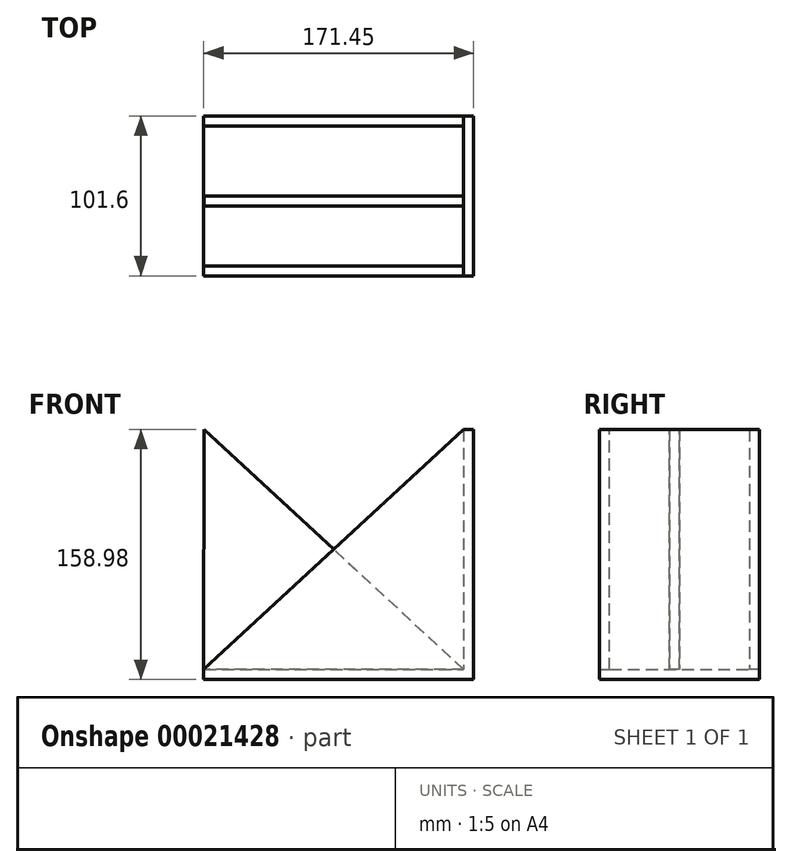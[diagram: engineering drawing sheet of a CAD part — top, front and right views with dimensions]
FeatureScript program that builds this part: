
annotation { "Feature Type Name" : "Feature", "Feature Type Description" : "" }
export const myFeature = defineFeature(function(context is Context, id is Id, definition is map)
    precondition{}
    {
        {
            var Q0;
            Q0=qCreatedBy(makeId("Front.planeOp"),FACE);
            var sketch = newSketch(context, id + "F0", { "sketchPlane" : qUnion([Q0])});
            skLineSegment(sketch, "E0", {"start": v(99.3, 82.76) * mm, "end": v(99.3, -69.64) * mm});
            skLineSegment(sketch, "E1", {"start": v(99.3, -69.64) * mm, "end": v(-65.8, -69.64) * mm});
            skLineSegment(sketch, "E2", {"start": v(-65.8, -69.64) * mm, "end": v(99.3, 82.76) * mm});
            skSolve(sketch);
        }
        {
            var Q0;
            Q0 = qSketchRegion(id + "F0", true);
            extrude(context, id + "F1", {"entities" : qUnion([Q0]), "depth" : 6.35 * mm});
        }
        {
            var Q0;
            Q0=makeQuery(id+"F1.opExtrude","SWEPT_FACE",FACE,{"disambiguationData":[OSD([sQuery(id+"F0.wireOp",EDGE,"E0")])]});
            var sketch = newSketch(context, id + "F2", { "sketchPlane" : qUnion([Q0])});
            skLineSegment(sketch, "E3.bottom", {"start": v(-6.35, 82.76) * mm, "end": v(38.1, 82.76) * mm});
            skLineSegment(sketch, "E3.top", {"start": v(-6.35, -69.64) * mm, "end": v(38.1, -69.64) * mm});
            skLineSegment(sketch, "E3.left", {"start": v(-6.35, 82.76) * mm, "end": v(-6.35, -69.64) * mm});
            skLineSegment(sketch, "E3.right", {"start": v(38.1, 82.76) * mm, "end": v(38.1, -69.64) * mm});
            skSolve(sketch);
        }
        {
            var Q0;
            Q0 = qSketchRegion(id + "F2", true);
            extrude(context, id + "F3", {"entities" : qUnion([Q0]), "operationType" : NewBodyOperationType.ADD, "depth" : 6.35 * mm});
        }
        {
            var Q0;
            Q0=makeQuery(id+"F3.opExtrude","SWEPT_FACE",FACE,{"disambiguationData":[OSD([sQuery(id+"F2.wireOp",EDGE,"E3.right")])]});
            var sketch = newSketch(context, id + "F4", { "sketchPlane" : qUnion([Q0])});
            skLineSegment(sketch, "E4", {"start": v(-99.3, -69.64) * mm, "end": v(65.59, 82.99) * mm});
            skLineSegment(sketch, "E5", {"start": v(65.59, 82.99) * mm, "end": v(65.8, -69.41) * mm});
            skLineSegment(sketch, "E6", {"start": v(65.8, -69.41) * mm, "end": v(-99.3, -69.64) * mm});
            skSolve(sketch);
        }
        {
            var Q0;
            Q0 = qSketchRegion(id + "F4", true);
            extrude(context, id + "F5", {"entities" : qUnion([Q0]), "operationType" : NewBodyOperationType.ADD, "depth" : 6.35 * mm});
        }
        {
            var Q0;
            Q0=makeQuery(id+"F3.opExtrude","CAP_FACE",FACE,{"disambiguationData":[OSD([sQuery(id+"F2.wireOp",EDGE,"E3.bottom"),sQuery(id+"F2.wireOp",EDGE,"E3.top"),sQuery(id+"F2.wireOp",EDGE,"E3.left"),sQuery(id+"F2.wireOp",EDGE,"E3.right")])],"isStart":false});
            var sketch = newSketch(context, id + "F6", { "sketchPlane" : qUnion([Q0])});
            skLineSegment(sketch, "E7.bottom", {"start": v(38.1, 82.76) * mm, "end": v(88.9, 82.76) * mm});
            skLineSegment(sketch, "E7.top", {"start": v(38.1, -69.64) * mm, "end": v(88.9, -69.64) * mm});
            skLineSegment(sketch, "E7.left", {"start": v(38.1, 82.76) * mm, "end": v(38.1, -69.64) * mm});
            skLineSegment(sketch, "E7.right", {"start": v(88.9, 82.76) * mm, "end": v(88.9, -69.64) * mm});
            skSolve(sketch);
        }
        {
            var Q0;
            Q0 = qSketchRegion(id + "F6", true);
            extrude(context, id + "F7", {"entities" : qUnion([Q0]), "operationType" : NewBodyOperationType.ADD, "oppositeDirection" : true, "depth" : 6.35 * mm});
        }
        {
            var Q0;
            Q0=makeQuery(id+"F7.opExtrude","SWEPT_FACE",FACE,{"disambiguationData":[OSD([sQuery(id+"F6.wireOp",EDGE,"E7.right")])]});
            var sketch = newSketch(context, id + "F8", { "sketchPlane" : qUnion([Q0])});
            skLineSegment(sketch, "E8", {"start": v(-99.3, 82.76) * mm, "end": v(65.8, -69.64) * mm});
            skLineSegment(sketch, "E9", {"start": v(65.8, -69.64) * mm, "end": v(-99.3, -69.64) * mm});
            skLineSegment(sketch, "E10", {"start": v(-99.3, -69.64) * mm, "end": v(-99.3, 82.76) * mm});
            skSolve(sketch);
        }
        {
            var Q0;
            Q0 = qSketchRegion(id + "F8", true);
            extrude(context, id + "F9", {"entities" : qUnion([Q0]), "operationType" : NewBodyOperationType.ADD, "depth" : 6.35 * mm});
        }
        {
            var Q0;
            Q0=makeQuery(id+"F7.boolean.opBoolean","MERGE",FACE,{"derivedFrom":[makeQuery(id+"F3.opExtrude","CAP_FACE",FACE,{"disambiguationData":[OSD([sQuery(id+"F2.wireOp",EDGE,"E3.bottom"),sQuery(id+"F2.wireOp",EDGE,"E3.top"),sQuery(id+"F2.wireOp",EDGE,"E3.left"),sQuery(id+"F2.wireOp",EDGE,"E3.right")])],"isStart":false}),makeQuery(id+"F7.opExtrude","CAP_FACE",FACE,{"disambiguationData":[OSD([sQuery(id+"F6.wireOp",EDGE,"E7.bottom"),sQuery(id+"F6.wireOp",EDGE,"E7.top"),sQuery(id+"F6.wireOp",EDGE,"E7.left"),sQuery(id+"F6.wireOp",EDGE,"E7.right")])],"isStart":true})]});
            var sketch = newSketch(context, id + "F10", { "sketchPlane" : qUnion([Q0])});
            skLineSegment(sketch, "E11.bottom", {"start": v(88.9, 82.76) * mm, "end": v(95.25, 82.76) * mm});
            skLineSegment(sketch, "E11.top", {"start": v(88.9, -69.64) * mm, "end": v(95.25, -69.64) * mm});
            skLineSegment(sketch, "E11.left", {"start": v(88.9, 82.76) * mm, "end": v(88.9, -69.64) * mm});
            skLineSegment(sketch, "E11.right", {"start": v(95.25, 82.76) * mm, "end": v(95.25, -69.64) * mm});
            skSolve(sketch);
        }
        {
            var Q0;
            Q0 = qSketchRegion(id + "F10", true);
            extrude(context, id + "F11", {"entities" : qUnion([Q0]), "operationType" : NewBodyOperationType.ADD, "oppositeDirection" : true, "depth" : 6.35 * mm});
        }
        {
            var Q0;
            Q0=makeQuery(id+"F11.boolean.opBoolean","MERGE",FACE,{"derivedFrom":[makeQuery(id+"F7.boolean.opBoolean","MERGE",FACE,{"derivedFrom":[makeQuery(id+"F3.boolean.opBoolean","MERGE",FACE,{"derivedFrom":[makeQuery(id+"F1.opExtrude","SWEPT_FACE",FACE,{"disambiguationData":[OSD([sQuery(id+"F0.wireOp",EDGE,"E1")])]}),makeQuery(id+"F3.opExtrude","SWEPT_FACE",FACE,{"disambiguationData":[OSD([sQuery(id+"F2.wireOp",EDGE,"E3.top")])]})]}),makeQuery(id+"F7.opExtrude","SWEPT_FACE",FACE,{"disambiguationData":[OSD([sQuery(id+"F6.wireOp",EDGE,"E7.top")])]})]}),makeQuery(id+"F9.opExtrude","SWEPT_FACE",FACE,{"disambiguationData":[OSD([sQuery(id+"F8.wireOp",EDGE,"E9")])]}),makeQuery(id+"F11.opExtrude","SWEPT_FACE",FACE,{"disambiguationData":[OSD([sQuery(id+"F10.wireOp",EDGE,"E11.top")])]})]});
            var sketch = newSketch(context, id + "F12", { "sketchPlane" : qUnion([Q0])});
            skLineSegment(sketch, "E12.bottom", {"start": v(-65.8, 6.35) * mm, "end": v(105.66, 6.35) * mm});
            skLineSegment(sketch, "E12.top", {"start": v(-65.8, -95.25) * mm, "end": v(105.66, -95.25) * mm});
            skLineSegment(sketch, "E12.left", {"start": v(-65.8, 6.35) * mm, "end": v(-65.8, -95.25) * mm});
            skLineSegment(sketch, "E12.right", {"start": v(105.66, 6.35) * mm, "end": v(105.66, -95.25) * mm});
            skSolve(sketch);
        }
        {
            var Q0;
            Q0 = qSketchRegion(id + "F12", true);
            extrude(context, id + "F13", {"entities" : qUnion([Q0]), "operationType" : NewBodyOperationType.ADD, "depth" : 6.35 * mm});
        }
    });
